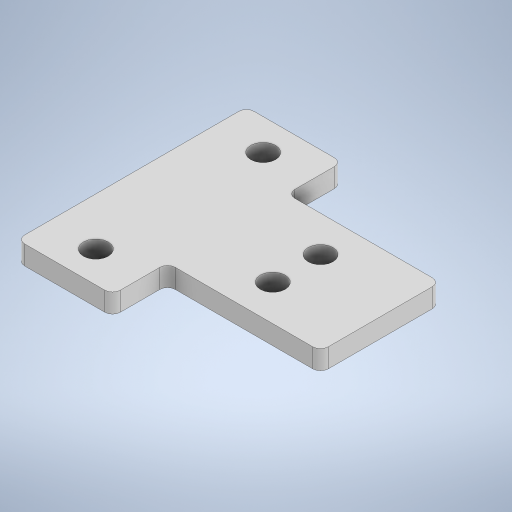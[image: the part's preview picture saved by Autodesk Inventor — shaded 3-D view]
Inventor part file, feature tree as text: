
AUTODESK INVENTOR PART (.ipt)
format: ipt  version: 2024.2 (Build 282272000, 272)  size: 253,440 bytes
history: native  units: mm
features: other x1, extrude x1, fillet x1, sketch x1
ambient origin geometry x8: Origin, YZ Plane, XZ Plane, XY Plane, X Axis, Y Axis, Z Axis, Center Point
bodies: Body1 (feature_tree)
feature tree (4):
  other  "Bryła1"
  extrude  "Wyciągnięcie proste1"  Depth=52.0mm
  fillet  "Zaokrąglenie1"  Radius=48.0mm
  sketch  "Szkic1"
